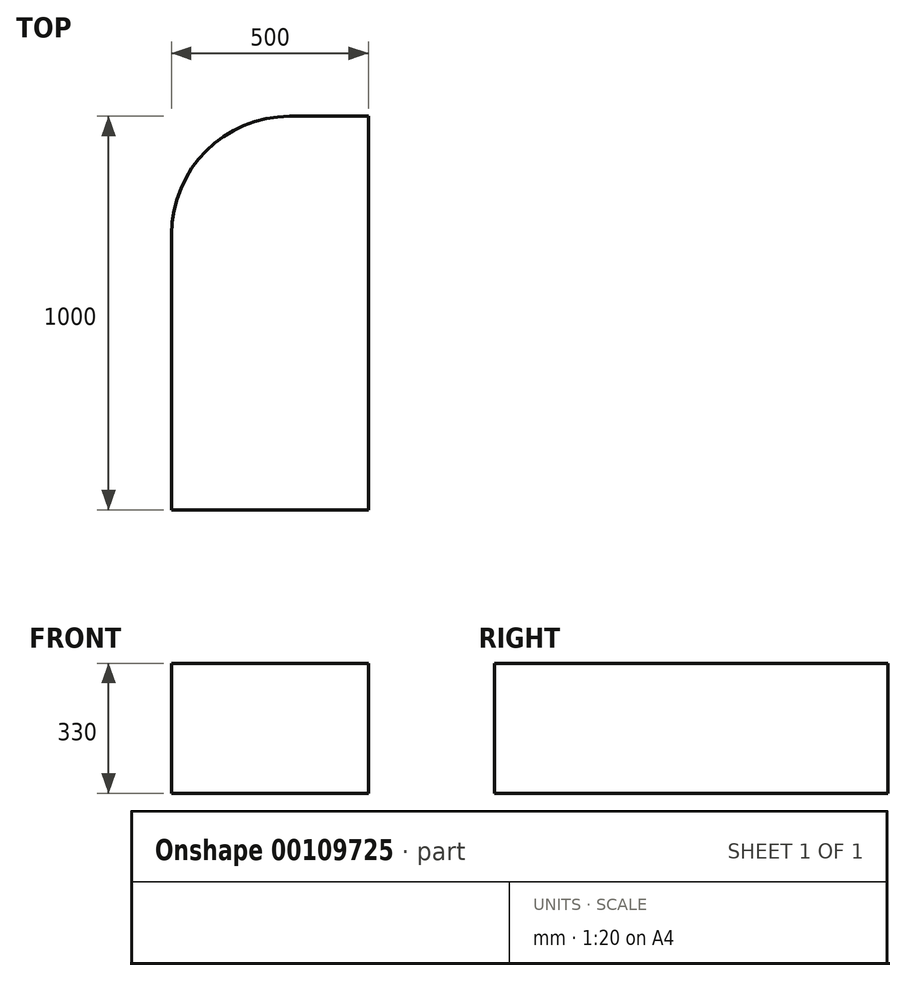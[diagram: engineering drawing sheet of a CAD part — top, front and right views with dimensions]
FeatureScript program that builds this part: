
annotation { "Feature Type Name" : "Feature", "Feature Type Description" : "" }
export const myFeature = defineFeature(function(context is Context, id is Id, definition is map)
    precondition{}
    {
        {
            var Q0;
            Q0=qCreatedBy(makeId("Top.planeOp"),FACE);
            var sketch = newSketch(context, id + "F0", { "sketchPlane" : qUnion([Q0])});
            skLineSegment(sketch, "E0.bottom", {"start": v(-649.19, 793.85) * mm, "end": v(-449.19, 793.85) * mm});
            skLineSegment(sketch, "E0.top", {"start": v(-949.19, -206.15) * mm, "end": v(-449.19, -206.15) * mm});
            skLineSegment(sketch, "E0.left", {"start": v(-949.19, 493.85) * mm, "end": v(-949.19, -206.15) * mm});
            skLineSegment(sketch, "E0.right", {"start": v(-449.19, 793.85) * mm, "end": v(-449.19, -206.15) * mm});
            skPoint(sketch, "E1.visualSharp", {"position": v(-949.19, 793.85) * mm});
            skArc(sketch, "E1.filletArc", {"start": v(-649.19, 793.85) * mm, "mid": v(-861.32, 705.99) * mm, "end": v(-949.19, 493.85) * mm});
            skSolve(sketch);
        }
        {
            var Q0;
            Q0=makeQuery(id+"F0.imprint","IMPRINT",FACE,{"disambiguationData":[TD([[makeQuery(id+"F0.imprint","IMPRINT",EDGE,{"derivedFrom":sQuery(id+"F0.wireOp",EDGE,"E0.bottom")}),-1.0]])]});
            extrude(context, id + "F1", {"entities" : qUnion([Q0]), "depth" : 330 * mm});
        }
    });
